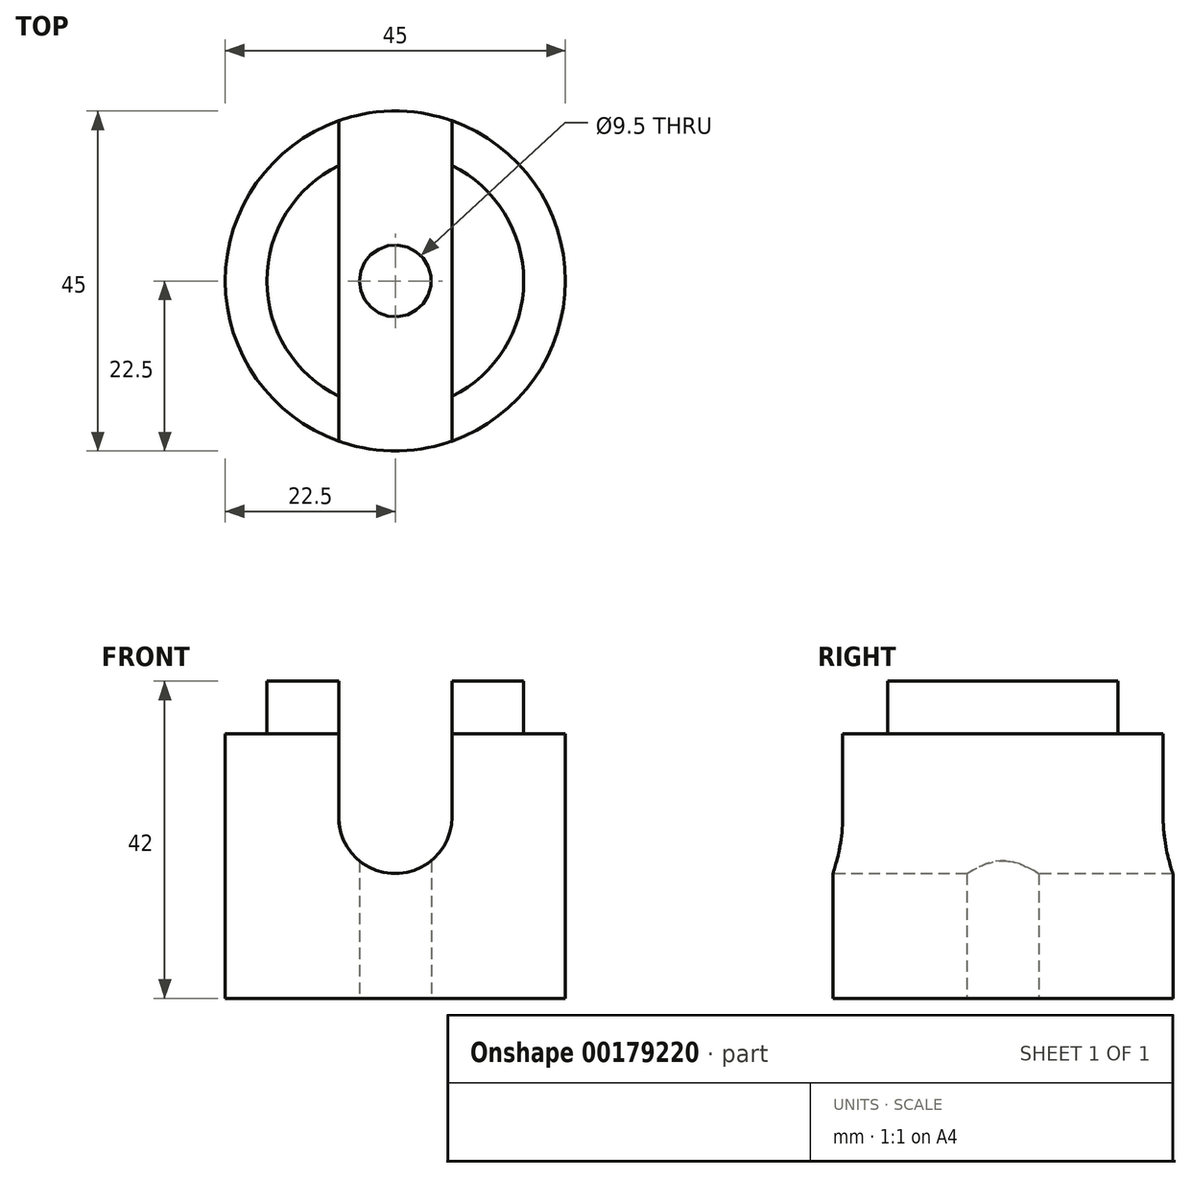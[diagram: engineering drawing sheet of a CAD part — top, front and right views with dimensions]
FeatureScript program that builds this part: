
annotation { "Feature Type Name" : "Feature", "Feature Type Description" : "" }
export const myFeature = defineFeature(function(context is Context, id is Id, definition is map)
    precondition{}
    {
        {
            var Q0;
            Q0=qCreatedBy(makeId("Front.planeOp"),FACE);
            var sketch = newSketch(context, id + "F0", { "sketchPlane" : qUnion([Q0])});
            skLineSegment(sketch, "E0", {"start": v(0, 0) * mm, "end": v(0, 29.09) * mm, "construction": true});
            skLineSegment(sketch, "E1", {"start": v(-4.75, 0) * mm, "end": v(-22.5, 0) * mm});
            skLineSegment(sketch, "E2", {"start": v(-22.5, 0) * mm, "end": v(-22.5, 35) * mm});
            skLineSegment(sketch, "E3", {"start": v(-22.5, 35) * mm, "end": v(-17, 35) * mm});
            skLineSegment(sketch, "E4", {"start": v(-17, 35) * mm, "end": v(-17, 42) * mm});
            skLineSegment(sketch, "E5", {"start": v(-17, 42) * mm, "end": v(-4.75, 42) * mm});
            skLineSegment(sketch, "E6", {"start": v(-4.75, 42) * mm, "end": v(-4.75, 0) * mm});
            skSolve(sketch);
        }
        {
            var Q0;
            Q0 = qSketchRegion(id + "F0", true);
            var Q1;
            Q1=sQuery(id+"F0.wireOp",EDGE,"E0");
            revolve(context, id + "F1", {"entities" : qUnion([Q0]), "axis" : qUnion([Q1]), "revolveType" : RevolveType.FULL});
        }
        {
            var Q0;
            Q0=qCreatedBy(makeId("Front.planeOp"),FACE);
            var sketch = newSketch(context, id + "F2", { "sketchPlane" : qUnion([Q0])});
            skArc(sketch, "E7", {"start": v(-7.5, 24) * mm, "mid": v(0, 16.5) * mm, "end": v(7.5, 24) * mm});
            skLineSegment(sketch, "E8", {"start": v(-7.5, 24) * mm, "end": v(-7.5, 56.58) * mm});
            skLineSegment(sketch, "E9", {"start": v(-7.5, 56.58) * mm, "end": v(7.5, 56.58) * mm});
            skLineSegment(sketch, "E10", {"start": v(7.5, 56.58) * mm, "end": v(7.5, 24) * mm});
            skSolve(sketch);
        }
        {
            var Q0;
            Q0 = qSketchRegion(id + "F2", true);
            extrude(context, id + "F3", {"entities" : qUnion([Q0]), "operationType" : NewBodyOperationType.REMOVE, "endBound" : BoundingType.THROUGH_ALL, "oppositeDirection" : true, "depth" : 25 * mm, "hasSecondDirection" : true, "secondDirectionBound" : SecondDirectionBoundingType.THROUGH_ALL, "secondDirectionOppositeDirection" : false, "secondDirectionDepth" : 25 * mm});
        }
    });
